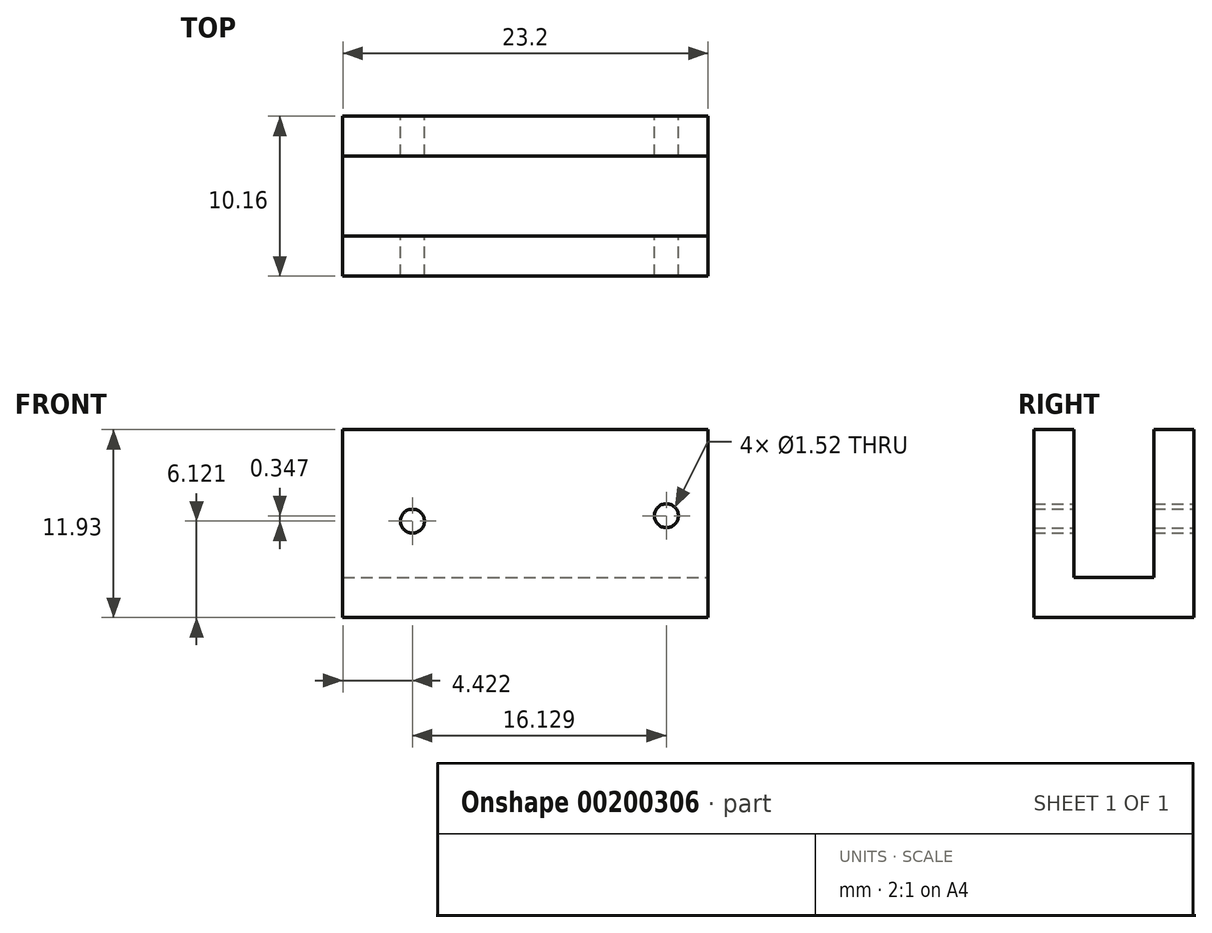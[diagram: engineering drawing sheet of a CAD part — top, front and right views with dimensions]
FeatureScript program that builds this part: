
annotation { "Feature Type Name" : "Feature", "Feature Type Description" : "" }
export const myFeature = defineFeature(function(context is Context, id is Id, definition is map)
    precondition{}
    {
        {
            var Q0;
            Q0=qCreatedBy(makeId("Front.planeOp"),FACE);
            var sketch = newSketch(context, id + "F0", { "sketchPlane" : qUnion([Q0])});
            skLineSegment(sketch, "E0.bottom", {"start": v(-58.14, 36.25) * mm, "end": v(-34.94, 36.25) * mm});
            skLineSegment(sketch, "E0.top", {"start": v(-58.14, 24.32) * mm, "end": v(-34.94, 24.32) * mm});
            skLineSegment(sketch, "E0.left", {"start": v(-58.14, 36.25) * mm, "end": v(-58.14, 24.32) * mm});
            skLineSegment(sketch, "E0.right", {"start": v(-34.94, 36.25) * mm, "end": v(-34.94, 24.32) * mm});
            skSolve(sketch);
        }
        {
            var Q0;
            Q0=makeQuery(id+"F0.imprint","IMPRINT",FACE,{"disambiguationData":[TD([[makeQuery(id+"F0.imprint","IMPRINT",EDGE,{"derivedFrom":sQuery(id+"F0.wireOp",EDGE,"E0.bottom")}),-1.0]])]});
            extrude(context, id + "F1", {"entities" : qUnion([Q0]), "depth" : 10.16 * mm});
        }
        {
            var Q0;
            Q0=makeQuery(id+"F1.opExtrude","SWEPT_FACE",FACE,{"disambiguationData":[OSD([sQuery(id+"F0.wireOp",EDGE,"E0.bottom")])]});
            var Q1;
            Q1=makeQuery(id+"F1.opExtrude","SWEPT_FACE",FACE,{"disambiguationData":[OSD([sQuery(id+"F0.wireOp",EDGE,"E0.left")])]});
            var Q2;
            Q2=makeQuery(id+"F1.opExtrude","SWEPT_FACE",FACE,{"disambiguationData":[OSD([sQuery(id+"F0.wireOp",EDGE,"E0.right")])]});
            shell(context, id + "F2", {"entities" : qUnion([Q0, Q1, Q2]), "thickness" : 2.54 * mm});
        }
        {
            var Q0;
            Q0=makeQuery(id+"F1.opExtrude","CAP_FACE",FACE,{"disambiguationData":[OSD([sQuery(id+"F0.wireOp",EDGE,"E0.bottom"),sQuery(id+"F0.wireOp",EDGE,"E0.top"),sQuery(id+"F0.wireOp",EDGE,"E0.left"),sQuery(id+"F0.wireOp",EDGE,"E0.right")])],"isStart":true});
            var sketch = newSketch(context, id + "F3", { "sketchPlane" : qUnion([Q0])});
            skCircle(sketch, "E1", {"center": v(37.59, 30.79) * mm, "radius": 1.48 * mm});
            skCircle(sketch, "E2", {"center": v(53.72, 30.44) * mm, "radius": 1.45 * mm});
            skSolve(sketch);
        }
        {
            var Q0;
            Q0=sQuery(id+"F3.wireOp",VERTEX,"E1.center");
            var Q1;
            Q1=sQuery(id+"F3.wireOp",VERTEX,"E2.center");
            var Q2;
            Q2=makeQuery(id+"F1.opExtrude","SWEPT_BODY",BODY,{"disambiguationData":[OSD([sQuery(id+"F0.wireOp",EDGE,"E0.bottom"),sQuery(id+"F0.wireOp",EDGE,"E0.top"),sQuery(id+"F0.wireOp",EDGE,"E0.left"),sQuery(id+"F0.wireOp",EDGE,"E0.right")])]});
            hole(context, id + "F4", {"style" : HoleStyle.SIMPLE, "endStyle" : HoleEndStyle.THROUGH, "holeDiameter" : 1.52 * mm, "locations" : qUnion([Q0, Q1]), "scope" : qUnion([Q2]), "isTappedThrough" : true});
        }
    });
